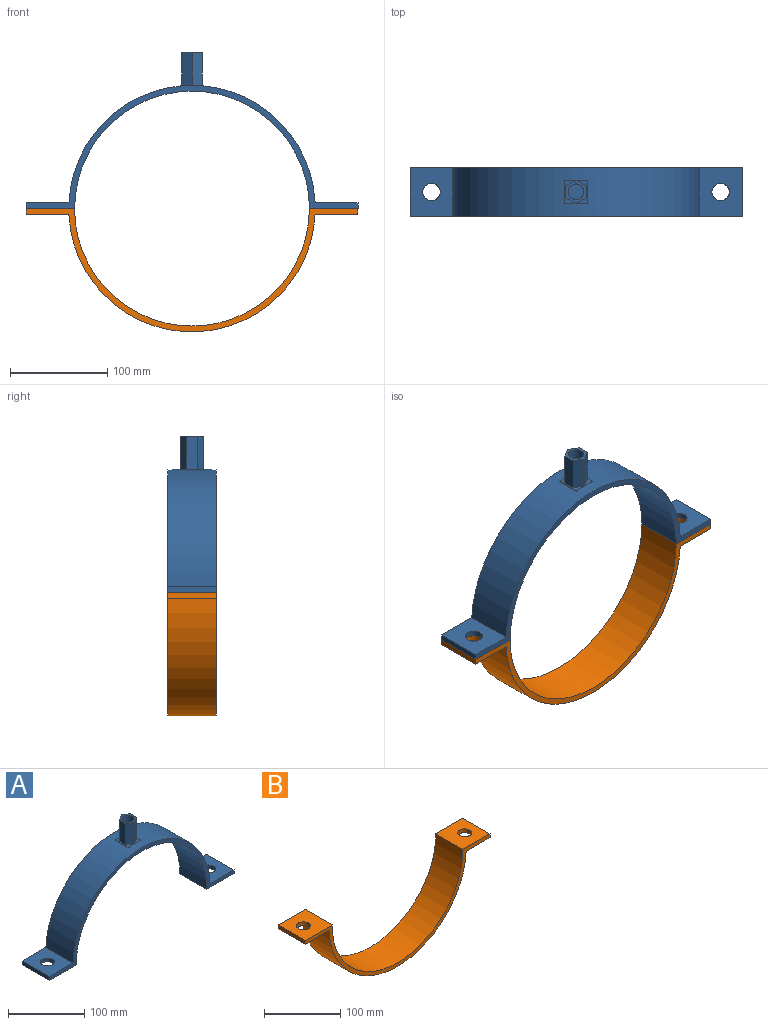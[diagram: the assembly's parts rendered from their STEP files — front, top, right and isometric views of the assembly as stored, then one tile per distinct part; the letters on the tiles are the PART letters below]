
ASSEMBLY  parts=2 mates=1
PART A: 29 faces, bbox 342x50x161 mm
  f0: plane 12x0.57mm, normal (0,-1,0), area 2.3mm2, adj f6,f16,f26
  f1: plane 12x0.57mm, normal (0,1,0), area 2.3mm2, adj f6,f16,f26
  f2: plane 24x0.57mm, normal (1,0,0), area 13.6mm2, adj f3,f4,f6,f22
  f3: plane 12x0.57mm, normal (0,-1,0), area 2.3mm2, adj f2,f6,f22
  f4: plane 12x0.57mm, normal (0,1,0), area 2.3mm2, adj f2,f6,f22
  f5: plane 50x44.14mm, normal (0,0,1), area 1952.6mm2, adj f6,f12,f13,f14,f17
  f6: cylinder r=127mm len=253.72mm, axis (0,1,0), area 18772mm2, adj f0,f1,f2,f3,f4,f5,f7,f13
  f7: plane 50x44.14mm, normal (0,0,1), area 1952.6mm2, adj f6,f8,f13,f14,f18
  f8: plane 50x6mm, normal (-1,0,0), area 300mm2, adj f7,f9,f13,f14
  f9: plane 50x50mm, normal (0,0,-1), area 2245.5mm2, adj f8,f10,f13,f14,f18
  f10: cylinder r=121mm len=242mm, axis (0,1,0), area 19006.6mm2, adj f9,f11,f13,f14
  f11: plane 50x50mm, normal (0,0,-1), area 2245.5mm2, adj f10,f12,f13,f14,f17
  f12: plane 50x6mm, normal (1,0,0), area 300mm2, adj f5,f11,f13,f14
  f13: plane 342x127mm, normal (0,-1,0), area 2865.9mm2, adj f5,f6,f7,f8,f9,f10,f11,f12
  f14: plane 342x127mm, normal (0,1,0), area 2865.9mm2, adj f5,f6,f7,f8,f9,f10,f11,f12
  f15: plane 24x20.78mm, normal (0,0,1), area 173.1mm2, adj f19,f20,f21,f23,f24,f25,f27
  f16: plane 24x0.57mm, normal (-1,0,0), area 13.6mm2, adj f0,f1,f6,f26
  f17: cylinder r=9mm len=18mm, axis (0,0,1), area 339.3mm2, adj f5,f11
  f18: cylinder r=9mm len=18mm, axis (0,0,1), area 339.3mm2, adj f7,f9
  f19: plane 34x10.39mm, normal (0.5,-0.87,0), area 408mm2, adj f15,f21,f22,f23
  f20: plane 34x10.39mm, normal (0.5,0.87,0), area 408mm2, adj f15,f21,f22,f25
  f21: plane 34x12mm, normal (1,0,0), area 408mm2, adj f15,f19,f20,f22
  f22: plane 24x12mm, normal (0,0,1), area 100.9mm2, adj f2,f3,f4,f19,f20,f21
  f23: plane 34x10.39mm, normal (-0.5,-0.87,0), area 408mm2, adj f15,f19,f24,f26
  f24: plane 34x12mm, normal (-1,0,0), area 408mm2, adj f15,f23,f25,f26
  f25: plane 34x10.39mm, normal (-0.5,0.87,0), area 408mm2, adj f15,f20,f24,f26
  f26: plane 24x12mm, normal (0,0,1), area 100.9mm2, adj f0,f1,f16,f23,f24,f25
  f27: cylinder r=8mm len=34mm, axis (0,0,1), area 1709mm2, adj f15,f28
  f28: plane 16x16mm, normal (0,0,1), area 201.1mm2, adj f27
PART B: 12 faces, bbox 342x50x127 mm
  f0: plane 50x50mm, normal (0,0,1), area 2245.5mm2, adj f1,f7,f8,f9,f10
  f1: cylinder r=121mm len=242mm, axis (0,1,0), area 19006.6mm2, adj f0,f2,f8,f9
  f2: plane 50x50mm, normal (0,0,1), area 2245.5mm2, adj f1,f3,f8,f9,f11
  f3: plane 50x6mm, normal (-1,0,0), area 300mm2, adj f2,f4,f8,f9
  f4: plane 50x44.14mm, normal (0,0,-1), area 1952.6mm2, adj f3,f5,f8,f9,f11
  f5: cylinder r=127mm len=253.72mm, axis (0,1,0), area 19348.9mm2, adj f4,f6,f8,f9
  f6: plane 50x44.14mm, normal (0,0,-1), area 1952.6mm2, adj f5,f7,f8,f9,f10
  f7: plane 50x6mm, normal (1,0,0), area 300mm2, adj f0,f6,f8,f9
  f8: plane 342x127mm, normal (0,-1,0), area 2865.9mm2, adj f0,f1,f2,f3,f4,f5,f6,f7
  f9: plane 342x127mm, normal (0,1,0), area 2865.9mm2, adj f0,f1,f2,f3,f4,f5,f6,f7
  f10: cylinder r=9mm len=18mm, axis (0,0,-1), area 339.3mm2, adj f0,f6
  f11: cylinder r=9mm len=18mm, axis (0,0,-1), area 339.3mm2, adj f2,f4
PLACE A t=(-47.21,27.01,8.15)mm
PLACE B t=(-47.28,27.01,8.15)mm
MATE fastened B.f11 <-> A.f18  axis (0,0,1) through (-196.21,27.01,8.15)mm
